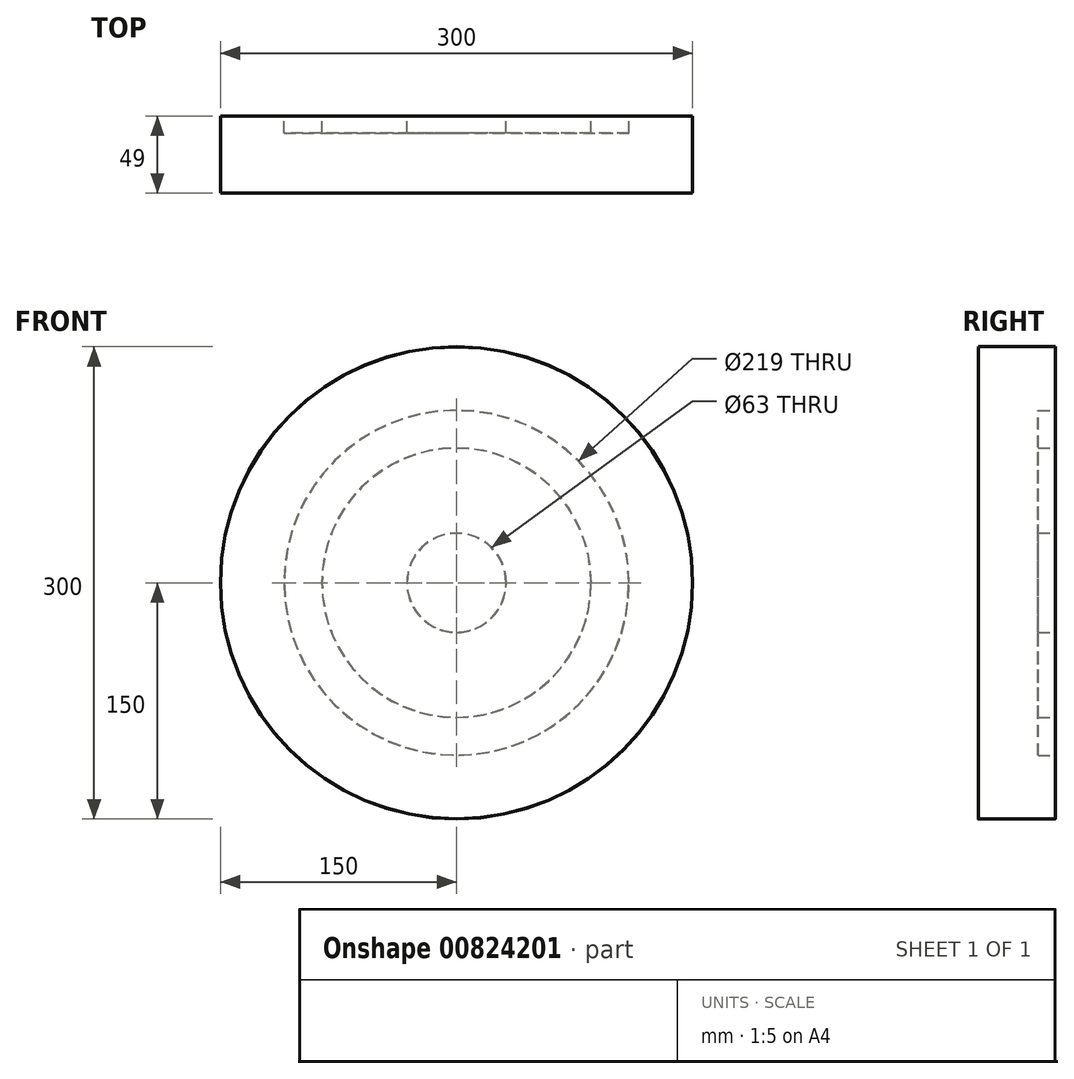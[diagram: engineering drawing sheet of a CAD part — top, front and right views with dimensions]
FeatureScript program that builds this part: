
annotation { "Feature Type Name" : "Feature", "Feature Type Description" : "" }
export const myFeature = defineFeature(function(context is Context, id is Id, definition is map)
    precondition{}
    {
        {
            var Q0;
            Q0=qCreatedBy(makeId("Front.planeOp"),FACE);
            var sketch = newSketch(context, id + "F0", { "sketchPlane" : qUnion([Q0])});
            skCircle(sketch, "E0", {"center": v(0, 0) * mm, "radius": 150 * mm});
            skSolve(sketch);
        }
        {
            var Q0;
            Q0=makeQuery(id+"F0.imprint","IMPRINT",FACE,{"disambiguationData":[TD([[makeQuery(id+"F0.imprint","IMPRINT",EDGE,{"derivedFrom":sQuery(id+"F0.wireOp",EDGE,"E0")}),1.0]])]});
            var Q1;
            Q1=makeQuery(id+"F0.imprint","IMPRINT",FACE,{"disambiguationData":[TD([[makeQuery(id+"F0.imprint","IMPRINT",EDGE,{"derivedFrom":sQuery(id+"F0.wireOp",EDGE,"wWX2iA8G-SRIu-dLJU-MbH4-nZh72lfMimyG")}),1.0]])]});
            var Q2;
            Q2=makeQuery(id+"F0.imprint","IMPRINT",FACE,{"disambiguationData":[TD([[makeQuery(id+"F0.imprint","IMPRINT",EDGE,{"derivedFrom":sQuery(id+"F0.wireOp",EDGE,"WBGFrGuJ-nkjN-w1pZ-qTBT-x1SGcq8tTcAd")}),1.0]])]});
            var Q3;
            Q3=makeQuery(id+"F0.imprint","IMPRINT",FACE,{"disambiguationData":[TD([[makeQuery(id+"F0.imprint","IMPRINT",EDGE,{"derivedFrom":sQuery(id+"F0.wireOp",EDGE,"CVNymvY4-LIkE-kObG-ShHJ-Mudy1xUb0FlA")}),1.0]])]});
            extrude(context, id + "F1", {"entities" : qUnion([Q0, Q1, Q2, Q3]), "depth" : 49 * mm, "offsetDistance" : 25 * mm});
        }
        {
            var Q0;
            Q0=qCreatedBy(makeId("Front.planeOp"),FACE);
            var sketch = newSketch(context, id + "F2", { "sketchPlane" : qUnion([Q0])});
            skCircle(sketch, "E1", {"center": v(0, 0) * mm, "radius": 109.5 * mm});
            skCircle(sketch, "E2", {"center": v(0, 0) * mm, "radius": 85.5 * mm});
            skCircle(sketch, "E3", {"center": v(0, 0) * mm, "radius": 31.5 * mm});
            skSolve(sketch);
        }
        {
            var Q0;
            Q0=makeQuery(id+"F2.imprint","IMPRINT",FACE,{"disambiguationData":[TD([[makeQuery(id+"F2.imprint","IMPRINT",EDGE,{"derivedFrom":sQuery(id+"F2.wireOp",EDGE,"E1")}),1.0]])]});
            var Q1;
            Q1=makeQuery(id+"F2.imprint","IMPRINT",FACE,{"disambiguationData":[TD([[makeQuery(id+"F2.imprint","IMPRINT",EDGE,{"derivedFrom":sQuery(id+"F2.wireOp",EDGE,"E3")}),1.0]])]});
            extrude(context, id + "F3", {"entities" : qUnion([Q0, Q1]), "operationType" : NewBodyOperationType.REMOVE, "depth" : 11 * mm, "offsetDistance" : 25 * mm});
        }
        {
            var Q0;
            Q0=makeQuery(id+"F1.opExtrude","CAP_EDGE",EDGE,{"disambiguationData":[OSD([sQuery(id+"F0.wireOp",EDGE,"E0")])],"isStart":true});
            var Q1;
            Q1=makeQuery(id+"F1.opExtrude","SWEPT_FACE",FACE,{"disambiguationData":[OSD([sQuery(id+"F0.wireOp",EDGE,"E0")])]});
            var Q2;
            Q2=makeQuery(id+"F3.boolean.opBoolean","COPY",EDGE,{"derivedFrom":makeQuery(id+"F3.opExtrude","CAP_EDGE",EDGE,{"disambiguationData":[OSD([sQuery(id+"F2.wireOp",EDGE,"E1")])],"isStart":true})});
            var Q3;
            Q3=makeQuery(id+"F3.boolean.opBoolean","COPY",FACE,{"derivedFrom":makeQuery(id+"F3.opExtrude","SWEPT_FACE",FACE,{"disambiguationData":[OSD([sQuery(id+"F2.wireOp",EDGE,"E1")])]})});
            var Q4;
            Q4=makeQuery(id+"F3.boolean.opBoolean","COPY",FACE,{"derivedFrom":makeQuery(id+"F3.opExtrude","CAP_FACE",FACE,{"disambiguationData":[OSD([sQuery(id+"F2.wireOp",EDGE,"E1"),sQuery(id+"F2.wireOp",EDGE,"E2")])],"isStart":false})});
            var Q5;
            Q5=makeQuery(id+"F3.boolean.opBoolean","COPY",EDGE,{"derivedFrom":makeQuery(id+"F3.opExtrude","CAP_EDGE",EDGE,{"disambiguationData":[OSD([sQuery(id+"F2.wireOp",EDGE,"E2")])],"isStart":true})});
            var Q6;
            Q6=makeQuery(id+"F3.boolean.opBoolean","COPY",FACE,{"derivedFrom":makeQuery(id+"F3.opExtrude","SWEPT_FACE",FACE,{"disambiguationData":[OSD([sQuery(id+"F2.wireOp",EDGE,"E2")])]})});
            var Q7;
            Q7=makeQuery(id+"F3.boolean.opBoolean","COPY",FACE,{"derivedFrom":makeQuery(id+"F3.opExtrude","SWEPT_FACE",FACE,{"disambiguationData":[OSD([sQuery(id+"F2.wireOp",EDGE,"E3")])]})});
            var Q8;
            Q8=makeQuery(id+"F3.boolean.opBoolean","COPY",EDGE,{"derivedFrom":makeQuery(id+"F3.opExtrude","CAP_EDGE",EDGE,{"disambiguationData":[OSD([sQuery(id+"F2.wireOp",EDGE,"E3")])],"isStart":true})});
            var Q9;
            {var subQ0=sQuery(id+"F0.wireOp",EDGE,"E0");Q9=makeQuery(id+"F3.boolean.opBoolean","SPLIT",FACE,{"disambiguationData":[TD([makeQuery(id+"F1.opExtrude","SWEPT_FACE",FACE,{"disambiguationData":[OSD([subQ0])]})])],"derivedFrom":makeQuery(id+"F1.opExtrude","CAP_FACE",FACE,{"disambiguationData":[OSD([subQ0])],"isStart":true})});}
            var Q10;
            Q10=makeQuery(id+"F3.boolean.opBoolean","SPLIT",FACE,{"disambiguationData":[TD([makeQuery(id+"F3.opExtrude","SWEPT_FACE",FACE,{"disambiguationData":[OSD([sQuery(id+"F2.wireOp",EDGE,"E2")])]})])],"derivedFrom":makeQuery(id+"F1.opExtrude","CAP_FACE",FACE,{"disambiguationData":[OSD([sQuery(id+"F0.wireOp",EDGE,"E0")])],"isStart":true})});
            var Q11;
            Q11=makeQuery(id+"F1.opExtrude","CAP_EDGE",EDGE,{"disambiguationData":[OSD([sQuery(id+"F0.wireOp",EDGE,"E0")])],"isStart":false});
            var Q12;
            Q12=makeQuery(id+"F1.opExtrude","CAP_FACE",FACE,{"disambiguationData":[OSD([sQuery(id+"F0.wireOp",EDGE,"E0")])],"isStart":false});
            var Q13;
            Q13=makeQuery(id+"F3.boolean.opBoolean","COPY",EDGE,{"derivedFrom":makeQuery(id+"F3.opExtrude","CAP_EDGE",EDGE,{"disambiguationData":[OSD([sQuery(id+"F2.wireOp",EDGE,"E1")])],"isStart":false})});
            var Q14;
            Q14=makeQuery(id+"F3.boolean.opBoolean","COPY",EDGE,{"derivedFrom":makeQuery(id+"F3.opExtrude","CAP_EDGE",EDGE,{"disambiguationData":[OSD([sQuery(id+"F2.wireOp",EDGE,"E2")])],"isStart":false})});
            var Q15;
            Q15=makeQuery(id+"F3.boolean.opBoolean","COPY",FACE,{"derivedFrom":makeQuery(id+"F3.opExtrude","CAP_FACE",FACE,{"disambiguationData":[OSD([sQuery(id+"F2.wireOp",EDGE,"E3")])],"isStart":false})});
            var Q16;
            Q16=makeQuery(id+"F3.boolean.opBoolean","COPY",EDGE,{"derivedFrom":makeQuery(id+"F3.opExtrude","CAP_EDGE",EDGE,{"disambiguationData":[OSD([sQuery(id+"F2.wireOp",EDGE,"E3")])],"isStart":false})});
            chamfer(context, id + "F4", {"entities" : qUnion([Q0, Q1, Q2, Q3, Q4, Q5, Q6, Q7, Q8, Q9, Q10, Q11, Q12, Q13, Q14, Q15, Q16]), "width" : 0.1 * mm, "tangentPropagation" : true});
        }
    });
